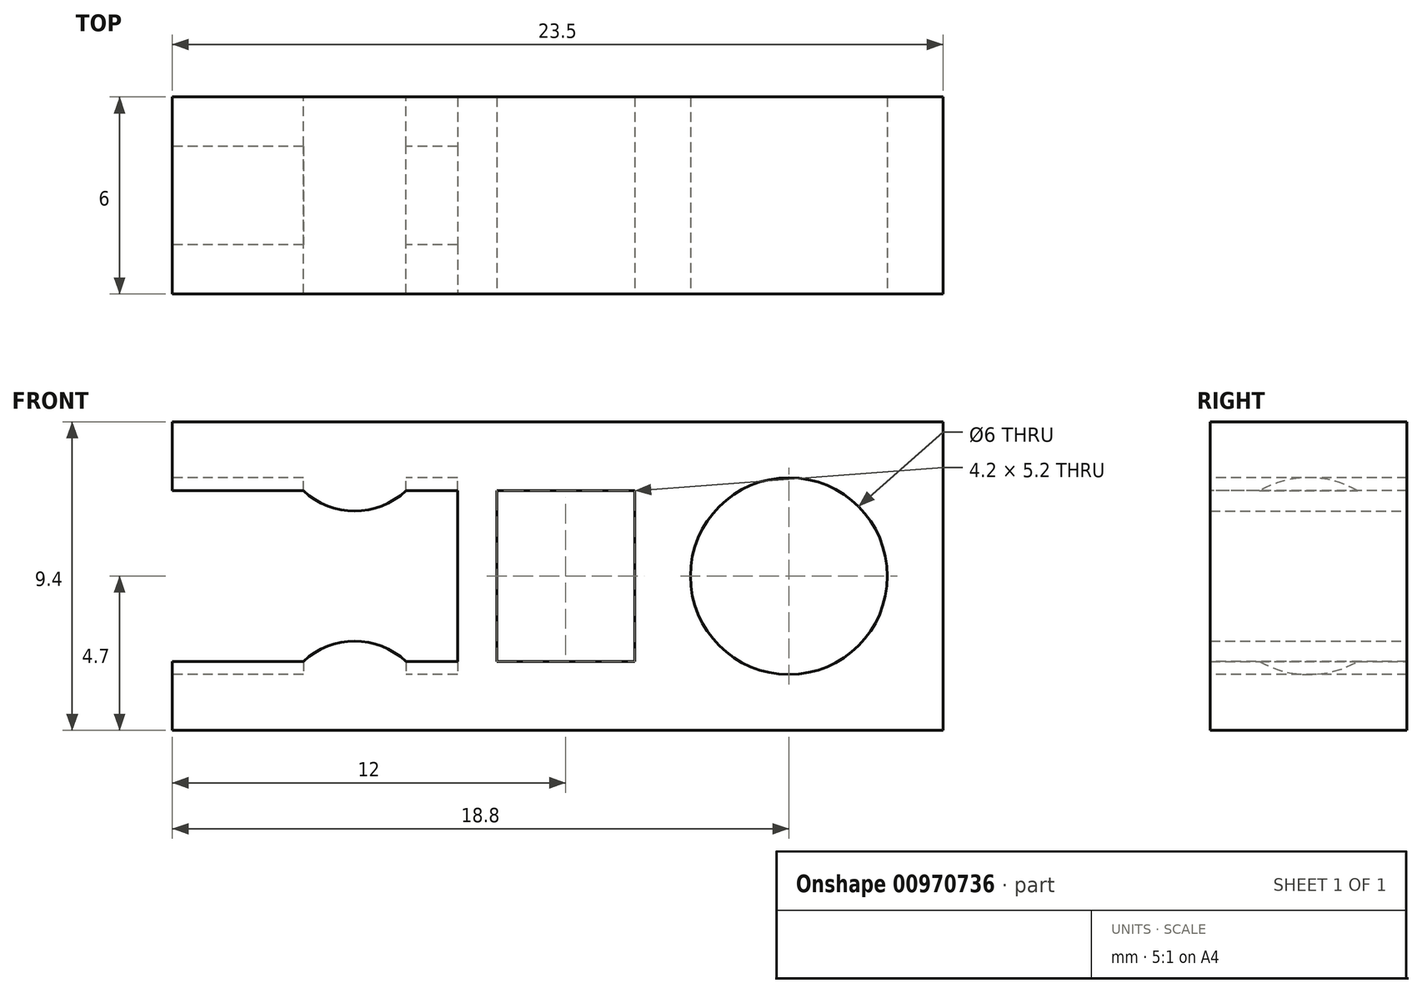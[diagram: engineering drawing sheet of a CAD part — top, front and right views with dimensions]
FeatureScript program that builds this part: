
annotation { "Feature Type Name" : "Feature", "Feature Type Description" : "" }
export const myFeature = defineFeature(function(context is Context, id is Id, definition is map)
    precondition{}
    {
        {
            var Q0;
            Q0=qCreatedBy(makeId("Front.planeOp"),FACE);
            var sketch = newSketch(context, id + "F0", { "sketchPlane" : qUnion([Q0])});
            skLineSegment(sketch, "E0", {"start": v(0, 7.38) * mm, "end": v(0, 0.76) * mm, "construction": true});
            skLineSegment(sketch, "E1", {"start": v(-24.9, 0) * mm, "end": v(10.18, 0) * mm, "construction": true});
            skLineSegment(sketch, "E2", {"start": v(-10.1, 0) * mm, "end": v(-10.1, -2.6) * mm});
            skLineSegment(sketch, "E3", {"start": v(-10.1, -2.6) * mm, "end": v(-11.67, -2.6) * mm});
            skLineSegment(sketch, "E4", {"start": v(-14.8, -2.6) * mm, "end": v(-18.8, -2.6) * mm});
            skLineSegment(sketch, "E5", {"start": v(-18.8, -2.6) * mm, "end": v(-18.8, -4.7) * mm});
            skLineSegment(sketch, "E6", {"start": v(-18.8, -4.7) * mm, "end": v(0, -4.7) * mm});
            skLineSegment(sketch, "E7", {"start": v(-3, 0) * mm, "end": v(-4.7, 0) * mm});
            skArc(sketch, "E8", {"start": v(-11.67, -2.6) * mm, "mid": v(-13.23, -1.99) * mm, "end": v(-14.8, -2.6) * mm, "construction": true});
            skLineSegment(sketch, "E9", {"start": v(-10.1, 0) * mm, "end": v(-8.9, 0) * mm});
            skLineSegment(sketch, "E10", {"start": v(-8.9, 0) * mm, "end": v(-8.9, -2.6) * mm});
            skLineSegment(sketch, "E11", {"start": v(-8.9, -2.6) * mm, "end": v(-4.7, -2.6) * mm});
            skLineSegment(sketch, "E12", {"start": v(-4.7, -2.6) * mm, "end": v(-4.7, 0) * mm});
            skLineSegment(sketch, "E13.trimOffspring", {"start": v(-4.7, 0) * mm, "end": v(-3, 0) * mm, "construction": true});
            skLineSegment(sketch, "E14.trimOffspring", {"start": v(-8.9, 0) * mm, "end": v(-10.1, 0) * mm});
            skArc(sketch, "E15", {"start": v(-3, 0) * mm, "mid": v(-2.12, -2.12) * mm, "end": v(0, -3) * mm});
            skLineSegment(sketch, "E16.trimOffspring", {"start": v(0, -3) * mm, "end": v(0, 0) * mm, "construction": true});
            skLineSegment(sketch, "E17", {"start": v(-11.67, -2.6) * mm, "end": v(-14.8, -2.6) * mm});
            skArc(sketch, "E18.MirrorCS", {"start": v(3, 0) * mm, "mid": v(2.12, -2.12) * mm, "end": v(0, -3) * mm});
            skLineSegment(sketch, "E19.MirrorCS", {"start": v(4.7, 0) * mm, "end": v(3, 0) * mm, "construction": true});
            skLineSegment(sketch, "E20", {"start": v(4.7, 0) * mm, "end": v(4.7, -4.7) * mm});
            skLineSegment(sketch, "E21", {"start": v(4.7, -4.7) * mm, "end": v(0, -4.7) * mm});
            skLineSegment(sketch, "E22", {"start": v(3, 0) * mm, "end": v(4.7, 0) * mm});
            skSolve(sketch);
        }
        {
            var Q0;
            Q0 = qSketchRegion(id + "F0", true);
            extrude(context, id + "F1", {"entities" : qUnion([Q0]), "endBound" : BoundingType.SYMMETRIC, "oppositeDirection" : true, "depth" : 6 * mm, "offsetDistance" : 25 * mm});
        }
        {
            var Q0;
            Q0=makeQuery(id+"F1.opExtrude","SWEPT_FACE",FACE,{"disambiguationData":[OSD([sQuery(id+"F0.wireOp",EDGE,"E5")])]});
            var sketch = newSketch(context, id + "F2", { "sketchPlane" : qUnion([Q0])});
            skArc(sketch, "E23", {"start": v(-1.5, -2.6) * mm, "mid": v(0, -3) * mm, "end": v(1.5, -2.6) * mm});
            skLineSegment(sketch, "E24", {"start": v(-1.5, -2.6) * mm, "end": v(1.5, -2.6) * mm});
            skSolve(sketch);
        }
        {
            var Q0;
            Q0 = qSketchRegion(id + "F2", true);
            var Q1;
            Q1=makeQuery(id+"F1.opExtrude","SWEPT_FACE",FACE,{"disambiguationData":[OSD([sQuery(id+"F0.wireOp",EDGE,"E2")])]});
            extrude(context, id + "F3", {"entities" : qUnion([Q0]), "operationType" : NewBodyOperationType.REMOVE, "endBound" : BoundingType.UP_TO_SURFACE, "oppositeDirection" : true, "depth" : 4 * mm, "endBoundEntityFace" : qUnion([Q1]), "offsetDistance" : 25 * mm});
        }
        {
            var Q0;
            Q0=makeQuery(id+"F1.opExtrude","CAP_FACE",FACE,{"disambiguationData":[OSD([sQuery(id+"F0.wireOp",EDGE,"E2"),sQuery(id+"F0.wireOp",EDGE,"E3"),sQuery(id+"F0.wireOp",EDGE,"E4"),sQuery(id+"F0.wireOp",EDGE,"E5"),sQuery(id+"F0.wireOp",EDGE,"E6"),sQuery(id+"F0.wireOp",EDGE,"E7"),sQuery(id+"F0.wireOp",EDGE,"E10"),sQuery(id+"F0.wireOp",EDGE,"E11"),sQuery(id+"F0.wireOp",EDGE,"E12"),sQuery(id+"F0.wireOp",EDGE,"E14.trimOffspring"),sQuery(id+"F0.wireOp",EDGE,"E15"),sQuery(id+"F0.wireOp",EDGE,"E16.trimOffspring"),sQuery(id+"F0.wireOp",EDGE,"E17")])],"isStart":false});
            var sketch = newSketch(context, id + "F4", { "sketchPlane" : qUnion([Q0])});
            skArc(sketch, "E25.1", {"start": v(11.67, -2.6) * mm, "mid": v(13.23, -1.99) * mm, "end": v(14.8, -2.6) * mm});
            skLineSegment(sketch, "E26", {"start": v(11.67, -2.6) * mm, "end": v(11.67, -4.7) * mm});
            skLineSegment(sketch, "E27", {"start": v(11.67, -4.7) * mm, "end": v(14.8, -4.7) * mm});
            skLineSegment(sketch, "E28", {"start": v(14.8, -4.7) * mm, "end": v(14.8, -2.6) * mm});
            skSolve(sketch);
        }
        {
            var Q0;
            Q0 = qSketchRegion(id + "F4", true);
            var Q1;
            Q1=makeQuery(id+"F1.opExtrude","CAP_FACE",FACE,{"disambiguationData":[OSD([sQuery(id+"F0.wireOp",EDGE,"E2"),sQuery(id+"F0.wireOp",EDGE,"E3"),sQuery(id+"F0.wireOp",EDGE,"E4"),sQuery(id+"F0.wireOp",EDGE,"E5"),sQuery(id+"F0.wireOp",EDGE,"E6"),sQuery(id+"F0.wireOp",EDGE,"E7"),sQuery(id+"F0.wireOp",EDGE,"E10"),sQuery(id+"F0.wireOp",EDGE,"E11"),sQuery(id+"F0.wireOp",EDGE,"E12"),sQuery(id+"F0.wireOp",EDGE,"E14.trimOffspring"),sQuery(id+"F0.wireOp",EDGE,"E15"),sQuery(id+"F0.wireOp",EDGE,"E16.trimOffspring"),sQuery(id+"F0.wireOp",EDGE,"E17")])],"isStart":true});
            extrude(context, id + "F5", {"entities" : qUnion([Q0]), "operationType" : NewBodyOperationType.ADD, "endBound" : BoundingType.UP_TO_SURFACE, "oppositeDirection" : true, "depth" : 25 * mm, "endBoundEntityFace" : qUnion([Q1]), "offsetDistance" : 25 * mm});
        }
        {
            var Q0;
            Q0=makeQuery(id+"F1.opExtrude","SWEPT_BODY",BODY,{"disambiguationData":[OSD([sQuery(id+"F0.wireOp",EDGE,"E2"),sQuery(id+"F0.wireOp",EDGE,"E3"),sQuery(id+"F0.wireOp",EDGE,"E4"),sQuery(id+"F0.wireOp",EDGE,"E5"),sQuery(id+"F0.wireOp",EDGE,"E6"),sQuery(id+"F0.wireOp",EDGE,"E7"),sQuery(id+"F0.wireOp",EDGE,"E10"),sQuery(id+"F0.wireOp",EDGE,"E11"),sQuery(id+"F0.wireOp",EDGE,"E12"),sQuery(id+"F0.wireOp",EDGE,"E14.trimOffspring"),sQuery(id+"F0.wireOp",EDGE,"E15"),sQuery(id+"F0.wireOp",EDGE,"E16.trimOffspring"),sQuery(id+"F0.wireOp",EDGE,"E17")])]});
            var Q1;
            Q1=qCreatedBy(makeId("Top.planeOp"),FACE);
            mirror(context, id + "F6", {"operationType" : NewBodyOperationType.ADD, "entities" : qUnion([Q0]), "mirrorPlane" : qUnion([Q1])});
        }
    });
